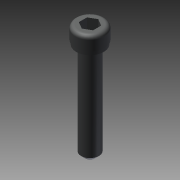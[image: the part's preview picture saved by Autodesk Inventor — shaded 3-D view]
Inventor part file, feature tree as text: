
AUTODESK INVENTOR PART (.ipt)
format: ipt  version: 2015 (Build 190159000, 159)  size: 117,760 bytes
history: native  units: in
note: dims shown in document units (in); Inventor stores cm internally (conversion verified against a paired STEP export)
features: other x6, extrude x1, chamfer x1, sketch x1
ambient origin geometry x8: Origin, YZ Plane, XZ Plane, XY Plane, X Axis, Y Axis, Z Axis, Center Point
bodies: Solid1 (feature_tree)
feature tree (9):
  other  "Screw 1.5in - 739195.ipt"
  extrude  "Extrusion1"  Depth=0.75in TaperAngle=0.0deg
  chamfer  "Chamfer1"  Distance=0.035in Angle=45.0deg
  other  "tetrix_739195_2013::Screw 1.5in - 739195.ipt"
  other  "TaggingFeature1"
  other  "FRONT"
  other  "TOP"
  other  "RIGHT"
  sketch  "Sketch1"  dims[d0=0.3937in d1=0.75in d2=0.0in d3=0.035in d4=0.125in d5=45.0deg]
